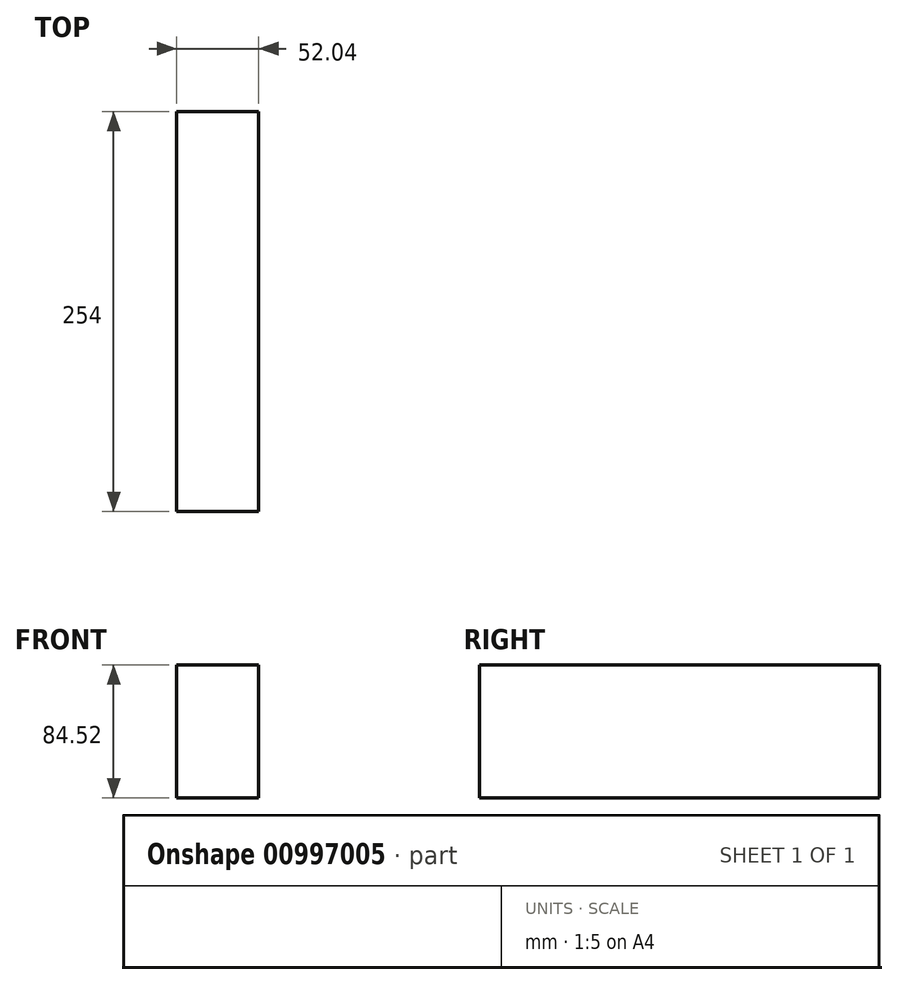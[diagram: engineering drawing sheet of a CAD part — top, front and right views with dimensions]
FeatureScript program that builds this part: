
annotation { "Feature Type Name" : "Feature", "Feature Type Description" : "" }
export const myFeature = defineFeature(function(context is Context, id is Id, definition is map)
    precondition{}
    {
        {
            var Q0;
            Q0=qCreatedBy(makeId("Front.planeOp"),FACE);
            var sketch = newSketch(context, id + "F0", { "sketchPlane" : qUnion([Q0])});
            skLineSegment(sketch, "E0.bottom", {"start": v(26.02, 42.26) * mm, "end": v(-26.02, 42.26) * mm});
            skLineSegment(sketch, "E0.top", {"start": v(26.02, -42.26) * mm, "end": v(-26.02, -42.26) * mm});
            skLineSegment(sketch, "E0.left", {"start": v(26.02, 42.26) * mm, "end": v(26.02, -42.26) * mm});
            skLineSegment(sketch, "E0.right", {"start": v(-26.02, 42.26) * mm, "end": v(-26.02, -42.26) * mm});
            skPoint(sketch, "E0.middle", {"position": v(0, 0) * mm});
            skSolve(sketch);
        }
        {
            var Q0;
            Q0=makeQuery(id+"F0.imprint","IMPRINT",FACE,{"disambiguationData":[TD([[makeQuery(id+"F0.imprint","IMPRINT",EDGE,{"derivedFrom":sQuery(id+"F0.wireOp",EDGE,"E0.bottom")}),1.0]])]});
            var sketch = newSketch(context, id + "F1", { "sketchPlane" : qUnion([Q0])});
            skSolve(sketch);
        }
        {
            var Q0;
            Q0 = qSketchRegion(id + "F1", true);
            var Q1;
            Q1=makeQuery(id+"F1.imprint","IMPRINT",FACE,{"disambiguationData":[TD([[makeQuery(id+"F1.imprint","IMPRINT",EDGE,{"derivedFrom":makeQuery(id+"F0.imprint","IMPRINT",EDGE,{"derivedFrom":sQuery(id+"F0.wireOp",EDGE,"E0.bottom")})}),1.0]])]});
            extrude(context, id + "F2", {"entities" : qUnion([Q0, Q1]), "endBound" : BoundingType.SYMMETRIC, "depth" : 254 * mm, "offsetDistance" : 25.4 * mm});
        }
    });
